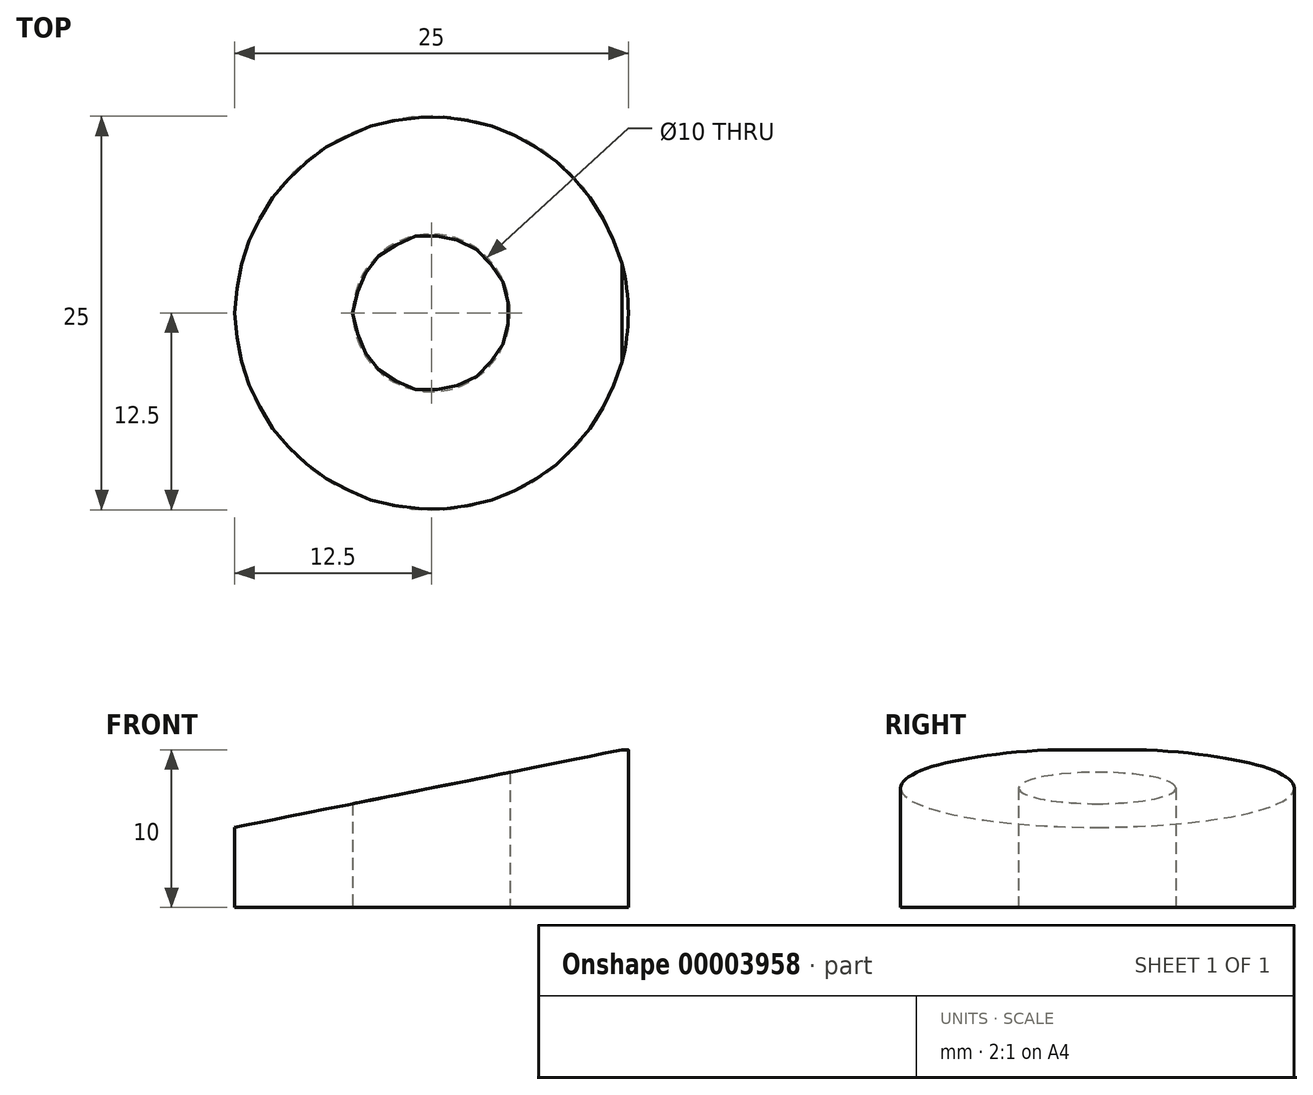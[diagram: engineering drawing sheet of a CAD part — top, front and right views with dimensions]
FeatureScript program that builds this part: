
annotation { "Feature Type Name" : "Feature", "Feature Type Description" : "" }
export const myFeature = defineFeature(function(context is Context, id is Id, definition is map)
    precondition{}
    {
        {
            var Q0;
            Q0=qCreatedBy(makeId("Front.planeOp"),FACE);
            var sketch = newSketch(context, id + "F0", { "sketchPlane" : qUnion([Q0])});
            skLineSegment(sketch, "E0", {"start": v(0, 0) * mm, "end": v(0, 10) * mm});
            skLineSegment(sketch, "E1", {"start": v(-5, 10) * mm, "end": v(-12.5, 10) * mm});
            skLineSegment(sketch, "E2", {"start": v(-12.5, 10) * mm, "end": v(-12.5, 0) * mm});
            skLineSegment(sketch, "E3", {"start": v(-12.5, 0) * mm, "end": v(-5, 0) * mm});
            skLineSegment(sketch, "E4", {"start": v(-5, 10) * mm, "end": v(-5, 0) * mm});
            skSolve(sketch);
        }
        {
            var Q0;
            Q0=makeQuery(id+"F0.imprint","IMPRINT",FACE,{"disambiguationData":[TD([[makeQuery(id+"F0.imprint","IMPRINT",EDGE,{"derivedFrom":sQuery(id+"F0.wireOp",EDGE,"E1")}),1.0]])]});
            var Q1;
            Q1=sQuery(id+"F0.wireOp",EDGE,"E0");
            revolve(context, id + "F1", {"entities" : qUnion([Q0]), "axis" : qUnion([Q1]), "revolveType" : RevolveType.FULL});
        }
        {
            var Q0;
            Q0=qCreatedBy(makeId("Front.planeOp"),FACE);
            var sketch = newSketch(context, id + "F2", { "sketchPlane" : qUnion([Q0])});
            skLineSegment(sketch, "E5.bottom", {"start": v(-12.5, 10.08) * mm, "end": v(12.5, 10.08) * mm});
            skLineSegment(sketch, "E5.left", {"start": v(-12.5, 10.08) * mm, "end": v(-12.5, 5.08) * mm});
            skLineSegment(sketch, "E6", {"start": v(-12.5, 5.08) * mm, "end": v(12.5, 10.08) * mm});
            skSolve(sketch);
        }
        {
            var Q0;
            Q0=makeQuery(id+"F2.imprint","IMPRINT",FACE,{"disambiguationData":[TD([[makeQuery(id+"F2.imprint","IMPRINT",EDGE,{"derivedFrom":sQuery(id+"F2.wireOp",EDGE,"E5.bottom")}),-1.0]])]});
            extrude(context, id + "F3", {"entities" : qUnion([Q0]), "operationType" : NewBodyOperationType.REMOVE, "endBound" : BoundingType.SYMMETRIC, "oppositeDirection" : true, "depth" : 25 * mm});
        }
    });
